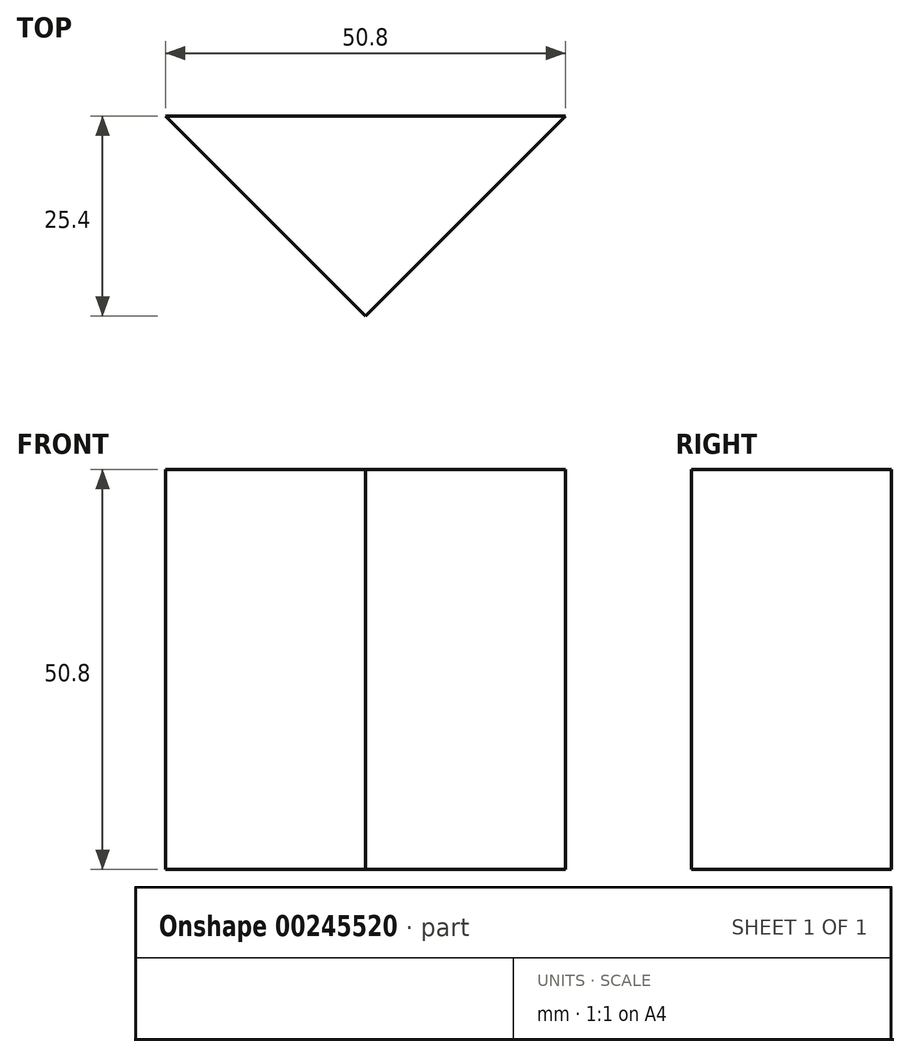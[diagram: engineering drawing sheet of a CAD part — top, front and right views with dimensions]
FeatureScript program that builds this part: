
annotation { "Feature Type Name" : "Feature", "Feature Type Description" : "" }
export const myFeature = defineFeature(function(context is Context, id is Id, definition is map)
    precondition{}
    {
        {
            var Q0;
            Q0=qCreatedBy(makeId("Front.planeOp"),FACE);
            var sketch = newSketch(context, id + "F0", { "sketchPlane" : qUnion([Q0])});
            skLineSegment(sketch, "E0.bottom", {"start": v(25.4, -25.4) * mm, "end": v(-25.4, -25.4) * mm});
            skLineSegment(sketch, "E0.top", {"start": v(25.4, 25.4) * mm, "end": v(-25.4, 25.4) * mm});
            skLineSegment(sketch, "E0.left", {"start": v(25.4, -25.4) * mm, "end": v(25.4, 25.4) * mm});
            skLineSegment(sketch, "E0.right", {"start": v(-25.4, -25.4) * mm, "end": v(-25.4, 25.4) * mm});
            skPoint(sketch, "E0.middle", {"position": v(0, 0) * mm});
            skLineSegment(sketch, "E1", {"start": v(25.4, 25.4) * mm, "end": v(0, 0) * mm});
            skLineSegment(sketch, "E2", {"start": v(25.4, -25.4) * mm, "end": v(0, 0) * mm});
            skLineSegment(sketch, "E3", {"start": v(-25.4, -25.4) * mm, "end": v(0, 0) * mm});
            skLineSegment(sketch, "E4", {"start": v(-25.4, 25.4) * mm, "end": v(0, 0) * mm});
            skSolve(sketch);
        }
        {
            var Q0;
            Q0=makeQuery(id+"F0.imprint","IMPRINT",FACE,{"disambiguationData":[TD([[makeQuery(id+"F0.imprint","IMPRINT",EDGE,{"derivedFrom":sQuery(id+"F0.wireOp",EDGE,"E0.right")}),-1.0]])]});
            extrude(context, id + "F1", {"entities" : qUnion([Q0]), "depth" : 25.4 * mm});
        }
        {
            var Q0;
            Q0=makeQuery(id+"F0.imprint","IMPRINT",FACE,{"disambiguationData":[TD([[makeQuery(id+"F0.imprint","IMPRINT",EDGE,{"derivedFrom":sQuery(id+"F0.wireOp",EDGE,"E0.top")}),1.0]])]});
            extrude(context, id + "F2", {"entities" : qUnion([Q0]), "operationType" : NewBodyOperationType.ADD, "depth" : 25.4 * mm});
        }
        {
            var Q0;
            Q0=makeQuery(id+"F0.imprint","IMPRINT",FACE,{"disambiguationData":[TD([[makeQuery(id+"F0.imprint","IMPRINT",EDGE,{"derivedFrom":sQuery(id+"F0.wireOp",EDGE,"E0.left")}),1.0]])]});
            extrude(context, id + "F3", {"entities" : qUnion([Q0]), "operationType" : NewBodyOperationType.ADD, "depth" : 25.4 * mm});
        }
        {
            var Q0;
            Q0=makeQuery(id+"F0.imprint","IMPRINT",FACE,{"disambiguationData":[TD([[makeQuery(id+"F0.imprint","IMPRINT",EDGE,{"derivedFrom":sQuery(id+"F0.wireOp",EDGE,"E0.bottom")}),-1.0]])]});
            extrude(context, id + "F4", {"entities" : qUnion([Q0]), "operationType" : NewBodyOperationType.ADD, "depth" : 25.4 * mm});
        }
        {
            var Q0;
            Q0=makeQuery(id+"F4.opExtrude","SWEPT_FACE",FACE,{"disambiguationData":[OSD([sQuery(id+"F0.wireOp",EDGE,"E0.bottom")])]});
            var sketch = newSketch(context, id + "F5", { "sketchPlane" : qUnion([Q0])});
            skPoint(sketch, "E5.start.orphan", {"position": v(0, 25.4) * mm});
            skLineSegment(sketch, "E6", {"start": v(0, 25.4) * mm, "end": v(-25.4, 0) * mm});
            skLineSegment(sketch, "E7", {"start": v(-25.4, 25.4) * mm, "end": v(-25.4, 0) * mm});
            skLineSegment(sketch, "E8", {"start": v(0, 25.4) * mm, "end": v(-25.4, 25.4) * mm});
            skSolve(sketch);
        }
        {
            var Q0;
            Q0 = qSketchRegion(id + "F5", true);
            extrude(context, id + "F6", {"entities" : qUnion([Q0]), "operationType" : NewBodyOperationType.REMOVE, "oppositeDirection" : true, "depth" : 50.8 * mm});
        }
        {
            var Q0;
            Q0=makeQuery(id+"F2.opExtrude","SWEPT_FACE",FACE,{"disambiguationData":[OSD([sQuery(id+"F0.wireOp",EDGE,"E0.top")])]});
            var sketch = newSketch(context, id + "F7", { "sketchPlane" : qUnion([Q0])});
            skLineSegment(sketch, "E9", {"start": v(0, -25.4) * mm, "end": v(25.4, 0) * mm});
            skLineSegment(sketch, "E10", {"start": v(0, -25.4) * mm, "end": v(25.4, -25.4) * mm});
            skLineSegment(sketch, "E11", {"start": v(25.4, -25.4) * mm, "end": v(25.4, 0) * mm});
            skSolve(sketch);
        }
        {
            var Q0;
            Q0 = qSketchRegion(id + "F7", true);
            extrude(context, id + "F8", {"entities" : qUnion([Q0]), "operationType" : NewBodyOperationType.REMOVE, "oppositeDirection" : true, "depth" : 50.8 * mm});
        }
    });
